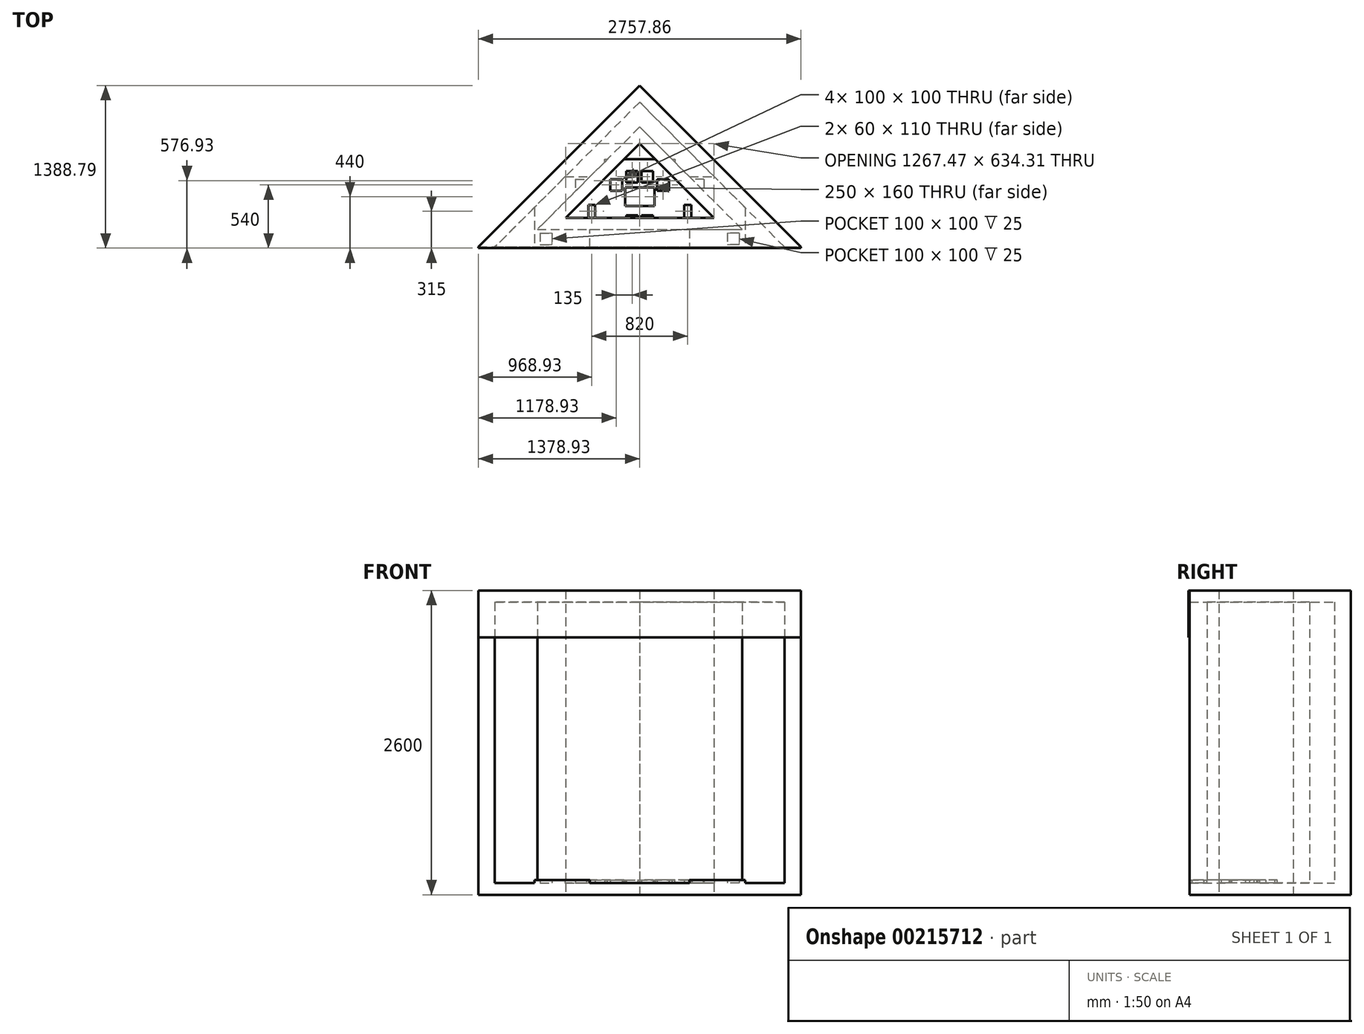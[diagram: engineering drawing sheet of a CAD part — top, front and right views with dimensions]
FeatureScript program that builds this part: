
annotation { "Feature Type Name" : "Feature", "Feature Type Description" : "" }
export const myFeature = defineFeature(function(context is Context, id is Id, definition is map)
    precondition{}
    {
        {
            var Q0;
            Q0=qCreatedBy(makeId("Top.planeOp"),FACE);
            var sketch = newSketch(context, id + "F0", { "sketchPlane" : qUnion([Q0])});
            skLineSegment(sketch, "E0", {"start": v(0, 1237.37) * mm, "end": v(-1237.5, 0) * mm});
            skLineSegment(sketch, "E1", {"start": v(-1237.5, 0) * mm, "end": v(1237.5, 0) * mm});
            skLineSegment(sketch, "E2", {"start": v(1237.5, 0) * mm, "end": v(0, 1237.37) * mm});
            skLineSegment(sketch, "E3", {"start": v(0, 1025.57) * mm, "end": v(-875, 149.77) * mm});
            skLineSegment(sketch, "E4", {"start": v(-875, 149.77) * mm, "end": v(875, 149.77) * mm});
            skLineSegment(sketch, "E5", {"start": v(875, 149.77) * mm, "end": v(0, 1025.57) * mm});
            skLineSegment(sketch, "E6", {"start": v(0, 149.77) * mm, "end": v(0, 0) * mm, "construction": true});
            skLineSegment(sketch, "E7", {"start": v(0.03, 1025.6) * mm, "end": v(-105.93, 1131.46) * mm, "construction": true});
            skLineSegment(sketch, "E8", {"start": v(0, 1025.57) * mm, "end": v(-1025.68, 0) * mm, "construction": true});
            skLineSegment(sketch, "E9", {"start": v(0, 1025.57) * mm, "end": v(1026.5, 0) * mm, "construction": true});
            skLineSegment(sketch, "E10", {"start": v(-501.48, 735.94) * mm, "end": v(-395.58, 630.03) * mm, "construction": true});
            skLineSegment(sketch, "E11", {"start": v(-425.61, 600) * mm, "end": v(425.96, 600) * mm, "construction": true});
            skLineSegment(sketch, "E12", {"start": v(-275.6, 750) * mm, "end": v(275.82, 750) * mm, "construction": true});
            skLineSegment(sketch, "E13", {"start": v(-300, 750) * mm, "end": v(-300, 600) * mm, "construction": true});
            skLineSegment(sketch, "E14.MirrorCS", {"start": v(300, 750) * mm, "end": v(300, 600) * mm, "construction": true});
            skLineSegment(sketch, "E15", {"start": v(-300, 600) * mm, "end": v(-300, 0) * mm, "construction": true});
            skLineSegment(sketch, "E16", {"start": v(-300, 0) * mm, "end": v(300, 0) * mm, "construction": true});
            skLineSegment(sketch, "E17", {"start": v(300, 0) * mm, "end": v(300, 600) * mm, "construction": true});
            skLineSegment(sketch, "E18", {"start": v(-900, 125.66) * mm, "end": v(-900, 0) * mm, "construction": true});
            skLineSegment(sketch, "E19", {"start": v(900, 126.39) * mm, "end": v(900, 0) * mm, "construction": true});
            skSolve(sketch);
        }
        {
            var Q0;
            Q0 = qSketchRegion(id + "F0", true);
            extrude(context, id + "F1", {"entities" : qUnion([Q0]), "depth" : 2400 * mm});
        }
        {
            var Q0;
            Q0=makeQuery(id+"F1.opExtrude","SWEPT_FACE",FACE,{"disambiguationData":[OSD([sQuery(id+"F0.wireOp",EDGE,"E1")])]});
            shell(context, id + "F2", {"entities" : qUnion([Q0]), "thickness" : 100 * mm, "oppositeDirection" : true});
        }
        {
            var Q0;
            Q0=makeQuery(id+"F1.opExtrude","SWEPT_FACE",FACE,{"disambiguationData":[OSD([sQuery(id+"F0.wireOp",EDGE,"E1")])]});
            var sketch = newSketch(context, id + "F3", { "sketchPlane" : qUnion([Q0])});
            skLineSegment(sketch, "E20.bottom", {"start": v(-1378.93, 2500) * mm, "end": v(1378.93, 2500) * mm});
            skLineSegment(sketch, "E20.top", {"start": v(-1378.93, 2100) * mm, "end": v(1378.93, 2100) * mm});
            skLineSegment(sketch, "E20.left", {"start": v(-1378.93, 2500) * mm, "end": v(-1378.93, 2100) * mm});
            skLineSegment(sketch, "E20.right", {"start": v(1378.93, 2500) * mm, "end": v(1378.93, 2100) * mm});
            skSolve(sketch);
        }
        {
            var Q0;
            Q0 = qSketchRegion(id + "F3", true);
            extrude(context, id + "F4", {"entities" : qUnion([Q0]), "operationType" : NewBodyOperationType.ADD, "depth" : 10 * mm});
        }
        {
            var Q0;
            {var subQ0=sQuery(id+"F0.wireOp",EDGE,"E2");var subQ1=sQuery(id+"F0.wireOp",EDGE,"E1");var subQ2=sQuery(id+"F0.wireOp",EDGE,"E0");Q0=makeQuery(id+"F2.opShell","OFFSET_FACE",FACE,{"disambiguationData":[OSD([subQ2,subQ1,subQ0]),TDD([makeQuery(id+"F1.opExtrude","CAP_FACE",FACE,{"disambiguationData":[OSD([subQ2,subQ1,subQ0])],"isStart":true})])]});}
            var sketch = newSketch(context, id + "F5", { "sketchPlane" : qUnion([Q0])});
            skLineSegment(sketch, "E21.left", {"start": v(-900, 337.47) * mm, "end": v(-900, 0) * mm});
            skLineSegment(sketch, "E21.right", {"start": v(900, 337.47) * mm, "end": v(900, 0) * mm});
            skLineSegment(sketch, "E22", {"start": v(-900, 337.47) * mm, "end": v(-637.44, 600) * mm});
            skLineSegment(sketch, "E23", {"start": v(637.44, 600) * mm, "end": v(900, 337.47) * mm});
            skLineSegment(sketch, "E24", {"start": v(-300, 600) * mm, "end": v(-300, 750) * mm});
            skLineSegment(sketch, "E25", {"start": v(-300, 750) * mm, "end": v(300, 750) * mm});
            skLineSegment(sketch, "E26", {"start": v(300, 750) * mm, "end": v(300, 600) * mm});
            skLineSegment(sketch, "E27", {"start": v(-637.44, 600) * mm, "end": v(-300, 600) * mm});
            skLineSegment(sketch, "E28", {"start": v(300, 600) * mm, "end": v(637.44, 600) * mm});
            skLineSegment(sketch, "E29", {"start": v(-900, 0) * mm, "end": v(-426.5, 0) * mm});
            skLineSegment(sketch, "E30", {"start": v(426.5, 0) * mm, "end": v(900, 0) * mm});
            skLineSegment(sketch, "E31", {"start": v(-426.5, 0) * mm, "end": v(-426.5, 150) * mm});
            skLineSegment(sketch, "E32", {"start": v(-426.5, 150) * mm, "end": v(426.5, 150) * mm});
            skLineSegment(sketch, "E33", {"start": v(426.5, 150) * mm, "end": v(426.5, 0) * mm});
            skLineSegment(sketch, "E34", {"start": v(-300, 600) * mm, "end": v(-300, 150) * mm, "construction": true});
            skLineSegment(sketch, "E35", {"start": v(300, 600) * mm, "end": v(300, 150) * mm, "construction": true});
            skLineSegment(sketch, "E36.bottom", {"start": v(-115, 270) * mm, "end": v(-15, 270) * mm});
            skLineSegment(sketch, "E36.top", {"start": v(-115, 170) * mm, "end": v(-15, 170) * mm});
            skLineSegment(sketch, "E36.left", {"start": v(-115, 270) * mm, "end": v(-115, 170) * mm});
            skLineSegment(sketch, "E36.right", {"start": v(-15, 270) * mm, "end": v(-15, 170) * mm});
            skLineSegment(sketch, "E37.bottom", {"start": v(-115, 650) * mm, "end": v(-15, 650) * mm});
            skLineSegment(sketch, "E37.top", {"start": v(-115, 550) * mm, "end": v(-15, 550) * mm});
            skLineSegment(sketch, "E37.left", {"start": v(-115, 650) * mm, "end": v(-115, 550) * mm});
            skLineSegment(sketch, "E37.right", {"start": v(-15, 650) * mm, "end": v(-15, 550) * mm});
            skLineSegment(sketch, "E38.bottom", {"start": v(-250, 580) * mm, "end": v(-150, 580) * mm});
            skLineSegment(sketch, "E38.top", {"start": v(-250, 480) * mm, "end": v(-150, 480) * mm});
            skLineSegment(sketch, "E38.left", {"start": v(-250, 580) * mm, "end": v(-250, 480) * mm});
            skLineSegment(sketch, "E38.right", {"start": v(-150, 580) * mm, "end": v(-150, 480) * mm});
            skLineSegment(sketch, "E39.bottom", {"start": v(-550, 580) * mm, "end": v(-450, 580) * mm});
            skLineSegment(sketch, "E39.top", {"start": v(-550, 480) * mm, "end": v(-450, 480) * mm});
            skLineSegment(sketch, "E39.left", {"start": v(-550, 580) * mm, "end": v(-550, 480) * mm});
            skLineSegment(sketch, "E39.right", {"start": v(-450, 580) * mm, "end": v(-450, 480) * mm});
            skLineSegment(sketch, "E40.bottom", {"start": v(-850, 120) * mm, "end": v(-750, 120) * mm});
            skLineSegment(sketch, "E40.top", {"start": v(-850, 20) * mm, "end": v(-750, 20) * mm});
            skLineSegment(sketch, "E40.left", {"start": v(-850, 120) * mm, "end": v(-850, 20) * mm});
            skLineSegment(sketch, "E40.right", {"start": v(-750, 120) * mm, "end": v(-750, 20) * mm});
            skLineSegment(sketch, "E41.MirrorCS", {"start": v(115, 170) * mm, "end": v(15, 170) * mm});
            skLineSegment(sketch, "E42.MirrorCS", {"start": v(15, 270) * mm, "end": v(15, 170) * mm});
            skLineSegment(sketch, "E43.MirrorCS", {"start": v(115, 270) * mm, "end": v(15, 270) * mm});
            skLineSegment(sketch, "E44.MirrorCS", {"start": v(115, 270) * mm, "end": v(115, 170) * mm});
            skLineSegment(sketch, "E45.MirrorCS", {"start": v(115, 550) * mm, "end": v(15, 550) * mm});
            skLineSegment(sketch, "E46.MirrorCS", {"start": v(115, 650) * mm, "end": v(15, 650) * mm});
            skLineSegment(sketch, "E47.MirrorCS", {"start": v(115, 650) * mm, "end": v(115, 550) * mm});
            skLineSegment(sketch, "E48.MirrorCS", {"start": v(15, 650) * mm, "end": v(15, 550) * mm});
            skLineSegment(sketch, "E49.MirrorCS", {"start": v(250, 580) * mm, "end": v(150, 580) * mm});
            skLineSegment(sketch, "E50.MirrorCS", {"start": v(250, 580) * mm, "end": v(250, 480) * mm});
            skLineSegment(sketch, "E51.MirrorCS", {"start": v(250, 480) * mm, "end": v(150, 480) * mm});
            skLineSegment(sketch, "E52.MirrorCS", {"start": v(150, 580) * mm, "end": v(150, 480) * mm});
            skLineSegment(sketch, "E53.MirrorCS", {"start": v(550, 580) * mm, "end": v(450, 580) * mm});
            skLineSegment(sketch, "E54.MirrorCS", {"start": v(550, 580) * mm, "end": v(550, 480) * mm});
            skLineSegment(sketch, "E55.MirrorCS", {"start": v(550, 480) * mm, "end": v(450, 480) * mm});
            skLineSegment(sketch, "E56.MirrorCS", {"start": v(450, 580) * mm, "end": v(450, 480) * mm});
            skLineSegment(sketch, "E57.MirrorCS", {"start": v(850, 120) * mm, "end": v(850, 20) * mm});
            skLineSegment(sketch, "E58.MirrorCS", {"start": v(850, 120) * mm, "end": v(750, 120) * mm});
            skLineSegment(sketch, "E59.MirrorCS", {"start": v(750, 120) * mm, "end": v(750, 20) * mm});
            skLineSegment(sketch, "E60.MirrorCS", {"start": v(850, 20) * mm, "end": v(750, 20) * mm});
            skLineSegment(sketch, "E61.bottom", {"start": v(-440, 360) * mm, "end": v(-380, 360) * mm});
            skLineSegment(sketch, "E61.top", {"start": v(-440, 250) * mm, "end": v(-380, 250) * mm});
            skLineSegment(sketch, "E61.left", {"start": v(-440, 360) * mm, "end": v(-440, 250) * mm});
            skLineSegment(sketch, "E61.right", {"start": v(-380, 360) * mm, "end": v(-380, 250) * mm});
            skLineSegment(sketch, "E62.MirrorCS", {"start": v(440, 360) * mm, "end": v(440, 250) * mm});
            skLineSegment(sketch, "E63.MirrorCS", {"start": v(440, 360) * mm, "end": v(380, 360) * mm});
            skLineSegment(sketch, "E64.MirrorCS", {"start": v(380, 360) * mm, "end": v(380, 250) * mm});
            skLineSegment(sketch, "E65.MirrorCS", {"start": v(440, 250) * mm, "end": v(380, 250) * mm});
            skLineSegment(sketch, "E66.bottom", {"start": v(-125, 510) * mm, "end": v(125, 510) * mm});
            skLineSegment(sketch, "E66.top", {"start": v(-125, 350) * mm, "end": v(125, 350) * mm});
            skLineSegment(sketch, "E66.left", {"start": v(-125, 510) * mm, "end": v(-125, 350) * mm});
            skLineSegment(sketch, "E66.right", {"start": v(125, 510) * mm, "end": v(125, 350) * mm});
            skSolve(sketch);
        }
        {
            var Q0;
            Q0 = qSketchRegion(id + "F5", true);
            extrude(context, id + "F6", {"entities" : qUnion([Q0]), "operationType" : NewBodyOperationType.ADD, "depth" : 25 * mm});
        }
    });
